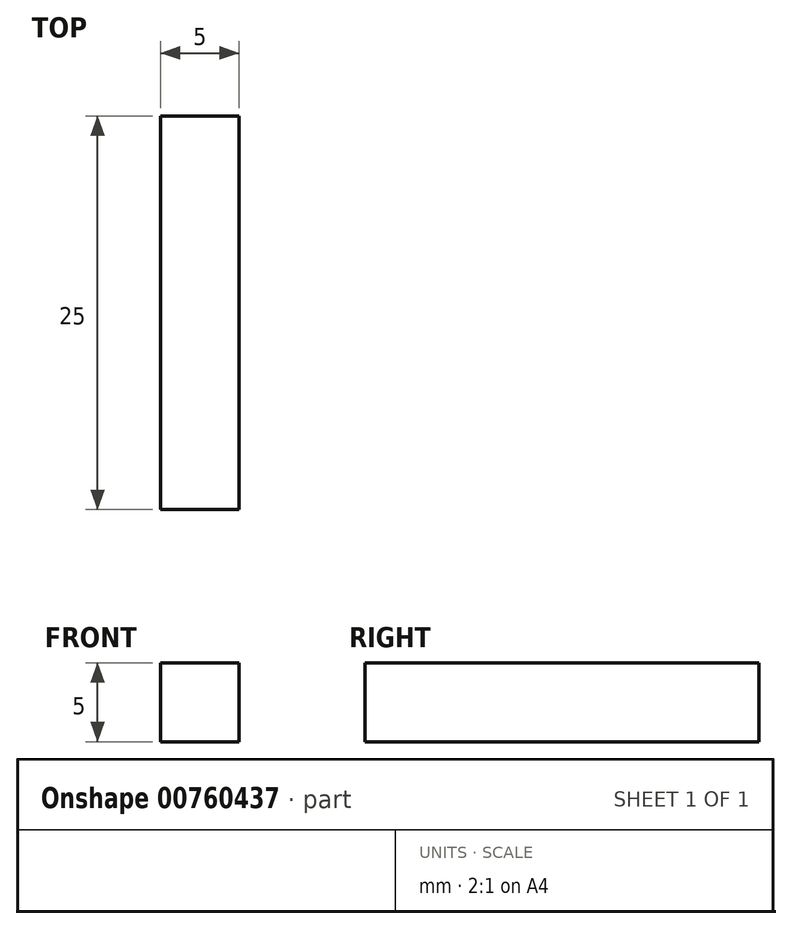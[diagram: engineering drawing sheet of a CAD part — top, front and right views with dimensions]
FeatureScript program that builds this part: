
annotation { "Feature Type Name" : "Feature", "Feature Type Description" : "" }
export const myFeature = defineFeature(function(context is Context, id is Id, definition is map)
    precondition{}
    {
        {
            var Q0;
            Q0=qCreatedBy(makeId("Front.planeOp"),FACE);
            var sketch = newSketch(context, id + "F0", { "sketchPlane" : qUnion([Q0])});
            skLineSegment(sketch, "E0.bottom", {"start": v(0, 0) * mm, "end": v(-5, 0) * mm});
            skLineSegment(sketch, "E0.top", {"start": v(0, 5) * mm, "end": v(-5, 5) * mm});
            skLineSegment(sketch, "E0.left", {"start": v(0, 0) * mm, "end": v(0, 5) * mm});
            skLineSegment(sketch, "E0.right", {"start": v(-5, 0) * mm, "end": v(-5, 5) * mm});
            skSolve(sketch);
        }
        {
            var Q0;
            Q0 = qSketchRegion(id + "F0", true);
            extrude(context, id + "F1", {"entities" : qUnion([Q0]), "depth" : 25 * mm, "offsetDistance" : 25.4 * mm});
        }
    });
